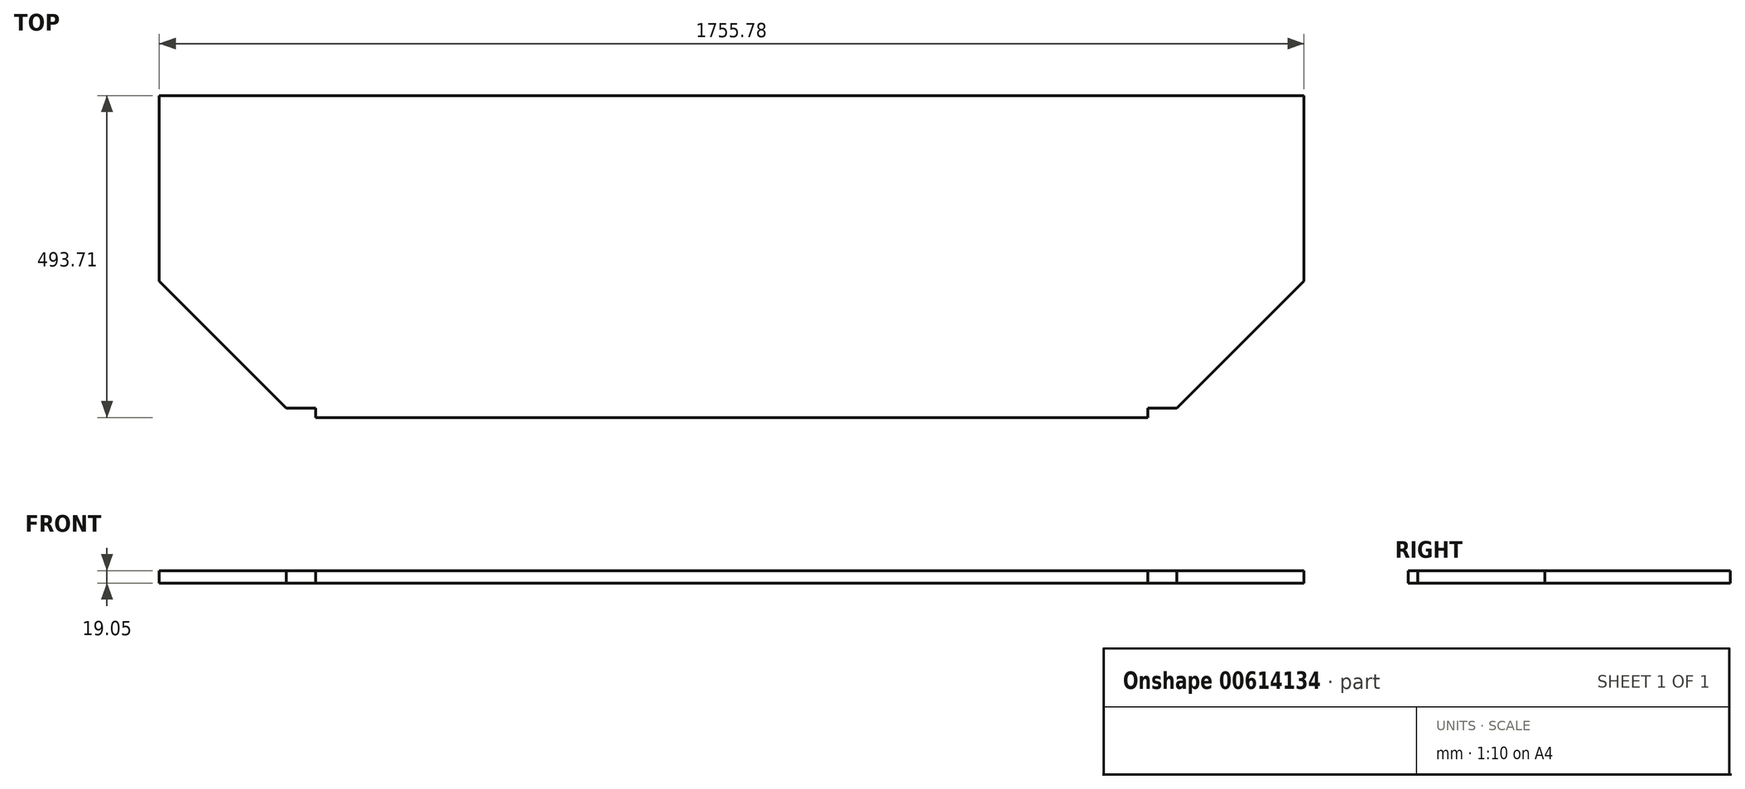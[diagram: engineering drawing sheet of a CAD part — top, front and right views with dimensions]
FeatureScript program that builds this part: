
annotation { "Feature Type Name" : "Feature", "Feature Type Description" : "" }
export const myFeature = defineFeature(function(context is Context, id is Id, definition is map)
    precondition{}
    {
        {
            var Q0;
            Q0=qCreatedBy(makeId("Top.planeOp"),FACE);
            var sketch = newSketch(context, id + "F0", { "sketchPlane" : qUnion([Q0])});
            skLineSegment(sketch, "E0.bottom", {"start": v(-15.16, 323.04) * mm, "end": v(857.97, 323.04) * mm});
            skLineSegment(sketch, "E0.top", {"start": v(-15.16, 304) * mm, "end": v(857.97, 304) * mm, "construction": true});
            skLineSegment(sketch, "E0.right", {"start": v(857.97, 323.04) * mm, "end": v(857.97, 304) * mm});
            skLineSegment(sketch, "E1", {"start": v(-15.16, 323.04) * mm, "end": v(-15.16, 26.13) * mm, "construction": true});
            skLineSegment(sketch, "E2", {"start": v(-15.16, 323.04) * mm, "end": v(-34.2, 323.04) * mm});
            skLineSegment(sketch, "E3", {"start": v(-34.2, 323.04) * mm, "end": v(-34.2, 18.24) * mm});
            skLineSegment(sketch, "E4", {"start": v(-34.2, 45.18) * mm, "end": v(176.89, -165.9) * mm, "construction": true});
            skLineSegment(sketch, "E5", {"start": v(-65.35, 49.39) * mm, "end": v(169, -184.96) * mm});
            skLineSegment(sketch, "E6", {"start": v(-15.16, 26.13) * mm, "end": v(-15.16, -97.24) * mm, "construction": true});
            skLineSegment(sketch, "E7", {"start": v(78.56, -94.53) * mm, "end": v(92.03, -81.06) * mm, "construction": true});
            skLineSegment(sketch, "E8.bottom", {"start": v(169, -184.96) * mm, "end": v(219.8, -184.96) * mm});
            skLineSegment(sketch, "E8.top", {"start": v(169, -165.9) * mm, "end": v(219.8, -165.9) * mm, "construction": true});
            skLineSegment(sketch, "E8.left", {"start": v(169, -184.96) * mm, "end": v(169, -165.9) * mm, "construction": true});
            skLineSegment(sketch, "E8.right", {"start": v(219.8, -184.96) * mm, "end": v(219.8, -165.9) * mm});
            skLineSegment(sketch, "E9", {"start": v(169, -184.96) * mm, "end": v(176.89, -165.9) * mm, "construction": true});
            skLineSegment(sketch, "E10", {"start": v(-34.2, 18.24) * mm, "end": v(-15.16, 26.13) * mm});
            skLineSegment(sketch, "E11", {"start": v(-15.16, 26.13) * mm, "end": v(176.89, -165.9) * mm});
            skLineSegment(sketch, "E12.MirrorCS", {"start": v(1750.14, 18.24) * mm, "end": v(1731.1, 26.13) * mm, "construction": true});
            skLineSegment(sketch, "E13.MirrorCS", {"start": v(1546.94, -184.96) * mm, "end": v(1539.05, -165.9) * mm, "construction": true});
            skLineSegment(sketch, "E14.MirrorCS", {"start": v(1546.94, -184.96) * mm, "end": v(1546.94, -165.9) * mm, "construction": true});
            skLineSegment(sketch, "E15.MirrorCS", {"start": v(1731.1, 323.04) * mm, "end": v(1750.14, 323.04) * mm});
            skLineSegment(sketch, "E16.MirrorCS", {"start": v(1496.14, -184.96) * mm, "end": v(1496.14, -165.9) * mm});
            skLineSegment(sketch, "E17.MirrorCS", {"start": v(1546.94, -165.9) * mm, "end": v(1496.14, -165.9) * mm, "construction": true});
            skLineSegment(sketch, "E18.MirrorCS", {"start": v(1546.94, -184.96) * mm, "end": v(1496.14, -184.96) * mm});
            skLineSegment(sketch, "E19.MirrorCS", {"start": v(1731.1, 26.13) * mm, "end": v(1539.05, -165.9) * mm});
            skLineSegment(sketch, "E20.MirrorCS", {"start": v(1637.38, -94.53) * mm, "end": v(1623.9, -81.06) * mm, "construction": true});
            skLineSegment(sketch, "E21.MirrorCS", {"start": v(1750.14, 45.18) * mm, "end": v(1539.05, -165.9) * mm, "construction": true});
            skLineSegment(sketch, "E22.MirrorCS", {"start": v(1731.1, 26.13) * mm, "end": v(1731.1, -97.24) * mm, "construction": true});
            skLineSegment(sketch, "E23.MirrorCS", {"start": v(1781.3, 49.39) * mm, "end": v(1546.94, -184.96) * mm});
            skLineSegment(sketch, "E24.MirrorCS", {"start": v(1750.14, 323.04) * mm, "end": v(1750.14, 18.24) * mm});
            skLineSegment(sketch, "E25.MirrorCS", {"start": v(1731.1, 323.04) * mm, "end": v(1731.1, 26.13) * mm, "construction": true});
            skLineSegment(sketch, "E26.MirrorCS", {"start": v(1731.1, 304) * mm, "end": v(857.97, 304) * mm});
            skLineSegment(sketch, "E27.MirrorCS", {"start": v(1731.1, 323.04) * mm, "end": v(857.97, 323.04) * mm});
            skLineSegment(sketch, "E28", {"start": v(-78.19, -25.74) * mm, "end": v(-34.2, 18.24) * mm});
            skLineSegment(sketch, "E29.0", {"start": v(163.9, -170.67) * mm, "end": v(224.9, -170.67) * mm});
            skLineSegment(sketch, "E30.0", {"start": v(-19.92, 320.37) * mm, "end": v(-19.92, 20.7) * mm});
            skLineSegment(sketch, "E31.0", {"start": v(-29.74, 308.75) * mm, "end": v(872.56, 308.75) * mm});
            skLineSegment(sketch, "E32.0", {"start": v(-35.79, 40.03) * mm, "end": v(178.8, -174.56) * mm});
            skLineSegment(sketch, "E33", {"start": v(194.4, -165.9) * mm, "end": v(194.4, -170.67) * mm, "construction": true});
            skLineSegment(sketch, "E34", {"start": v(80.87, -69.89) * mm, "end": v(77.5, -73.26) * mm, "construction": true});
            skLineSegment(sketch, "E35", {"start": v(421.4, 304) * mm, "end": v(421.4, 308.75) * mm, "construction": true});
            skLineSegment(sketch, "E36", {"start": v(-19.92, 159.04) * mm, "end": v(-15.16, 159.04) * mm, "construction": true});
            skLineSegment(sketch, "E37", {"start": v(857.97, 304) * mm, "end": v(857.97, 130.01) * mm, "construction": true});
            skLineSegment(sketch, "E38.MirrorCS", {"start": v(1745.68, 308.75) * mm, "end": v(843.38, 308.75) * mm});
            skLineSegment(sketch, "E39.MirrorCS", {"start": v(1735.86, 320.37) * mm, "end": v(1735.86, 20.7) * mm});
            skLineSegment(sketch, "E40.MirrorCS", {"start": v(1751.73, 40.03) * mm, "end": v(1537.14, -174.56) * mm});
            skLineSegment(sketch, "E41.MirrorCS", {"start": v(1552.05, -170.67) * mm, "end": v(1491.04, -170.67) * mm});
            skLineSegment(sketch, "E42", {"start": v(219.8, -184.96) * mm, "end": v(1496.14, -184.96) * mm});
            skSolve(sketch);
        }
        {
            var Q0;
            {var subQ15=sQuery(id+"F0.wireOp",EDGE,"E42");Q0=makeQuery(id+"F0.imprint","IMPRINT",FACE,{"disambiguationData":[TD([[makeQuery(id+"F0.imprint","IMPRINT",EDGE,{"derivedFrom":subQ15}),1.0]])]});}
            extrude(context, id + "F1", {"entities" : qUnion([Q0]), "depth" : 19.05 * mm, "offsetDistance" : 25.4 * mm});
        }
    });
